# Revit family: xxx
name_source: partatom
category: Generic Models
revit_build: Autodesk Revit MEP 2013 (Build: 20130531_2115(x64)
units: mm (PartAtom-declared; Revit-internal decimal feet)

## types (20) — shared parameters
Manufacturer = Zip Industries Ltd
Product Range = Hydrotap
URL = www.zipindustries.co.uk
WRAS Approved = Yes

## per-type parameters (varying)
| type | Model | Tap Colour |
| Hydrotap Elite - 93374UK (Bright Chrome) |  |  |
| Hydrotap Elite - 93380UK (Brushed Chrome) |  |  |
| Hydrotap Elite - 93386UK (Gloss Black) |  |  |
| Hydrotap Elite - 93392UK (Matt Black) |  |  |
| Hydrotap Elite - 93369UK (Bright Chrome) |  |  |
| Hydrotap Elite - 93375UK (Brushed Chrome) |  |  |
| Hydrotap Elite - 93381UK (Gloss Black) |  |  |
| Hydrotap Elite - 93387UK (Matt Black) |  |  |
| Hydrotap Elite - 93373UK (Bright Chrome) |  |  |
| Hydrotap Elite - 93379UK (Brushed Chrome) |  |  |
| Hydrotap Elite - 93385UK (Gloss Black) |  |  |
| Hydrotap Elite - 93391UK (Matt Black) |  |  |
| Hydrotap Elite - 93372UK (Bright Chrome) |  |  |
| Hydrotap Elite - 93378UK (Brushed Chrome) | Elite | As of the above  'name' List |
| Hydrotap Elite - 93384UK (Gloss Black) |  |  |
| Hydrotap Elite - 93390UK (Matt Black) |  |  |
| Hydrotap Elite - 93371UK (Bright Chrome) |  |  |
| Hydrotap Elite - 93377UK (Brushed Chrome) |  |  |
| Hydrotap Elite - 93383UK (Gloss Black) |  |  |
| Hydrotap Elite - 93389UK (Matt Black) |  |  |
